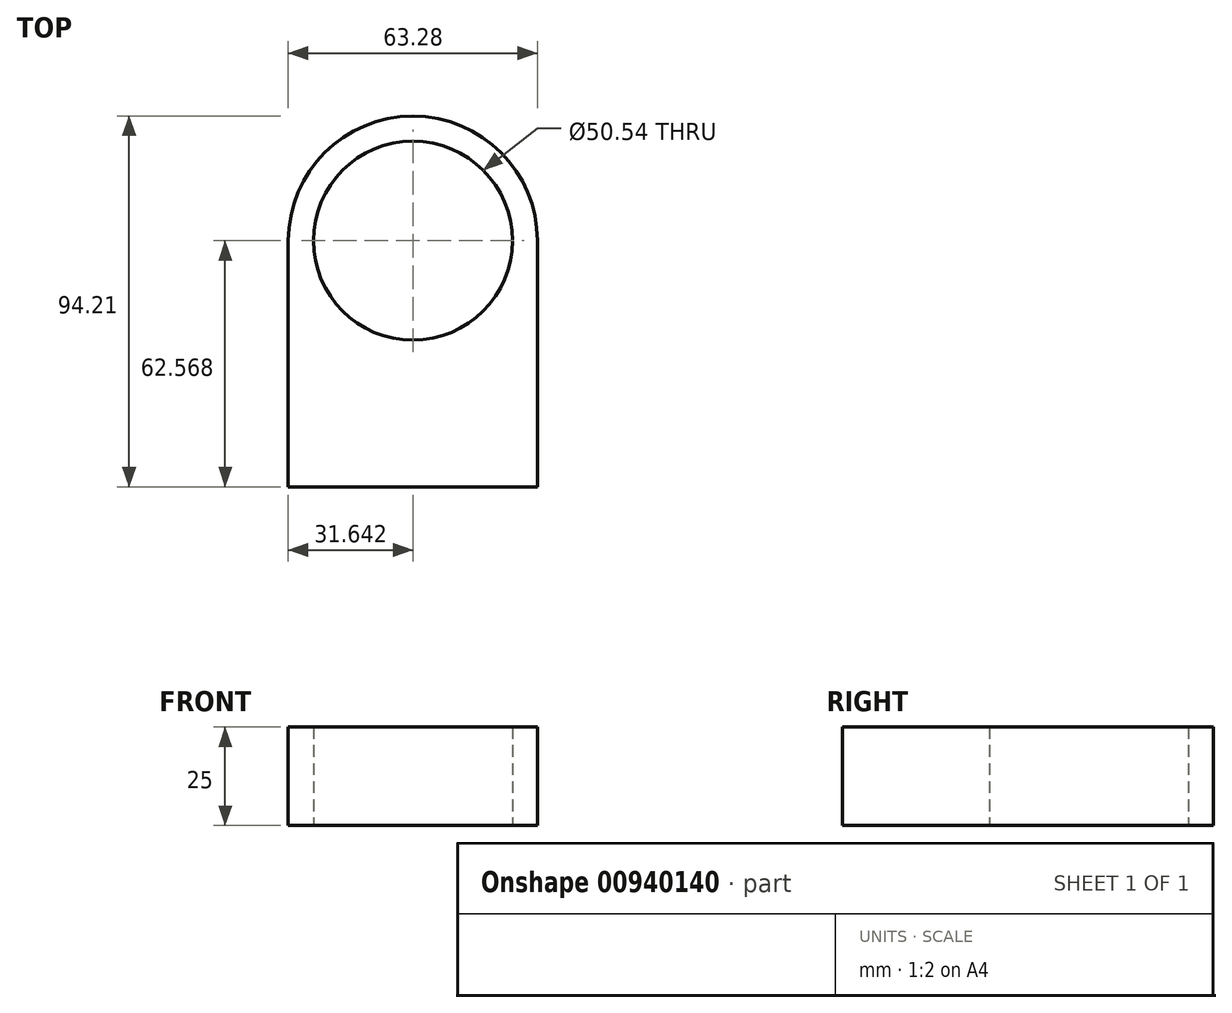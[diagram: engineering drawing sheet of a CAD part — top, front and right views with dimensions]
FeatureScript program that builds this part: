
annotation { "Feature Type Name" : "Feature", "Feature Type Description" : "" }
export const myFeature = defineFeature(function(context is Context, id is Id, definition is map)
    precondition{}
    {
        {
            var Q0;
            Q0=qCreatedBy(makeId("Top.planeOp"),FACE);
            var sketch = newSketch(context, id + "F0", { "sketchPlane" : qUnion([Q0])});
            skLineSegment(sketch, "E0.bottom", {"start": v(-28.43, -38.42) * mm, "end": v(34.85, -38.42) * mm});
            skLineSegment(sketch, "E0.left", {"start": v(-28.43, -38.42) * mm, "end": v(-28.43, 24.15) * mm});
            skLineSegment(sketch, "E0.right", {"start": v(34.85, -38.42) * mm, "end": v(34.85, 24.15) * mm});
            skArc(sketch, "E1", {"start": v(34.85, 24.15) * mm, "mid": v(3.21, 55.8) * mm, "end": v(-28.43, 24.15) * mm});
            skCircle(sketch, "E2", {"center": v(3.21, 24.15) * mm, "radius": 25.27 * mm});
            skSolve(sketch);
        }
        {
            var Q0;
            Q0=makeQuery(id+"F0.imprint","IMPRINT",FACE,{"disambiguationData":[TD([[makeQuery(id+"F0.imprint","IMPRINT",EDGE,{"derivedFrom":sQuery(id+"F0.wireOp",EDGE,"E0.bottom")}),1.0]])]});
            extrude(context, id + "F1", {"entities" : qUnion([Q0]), "depth" : 25 * mm, "offsetDistance" : 25 * mm});
        }
    });
